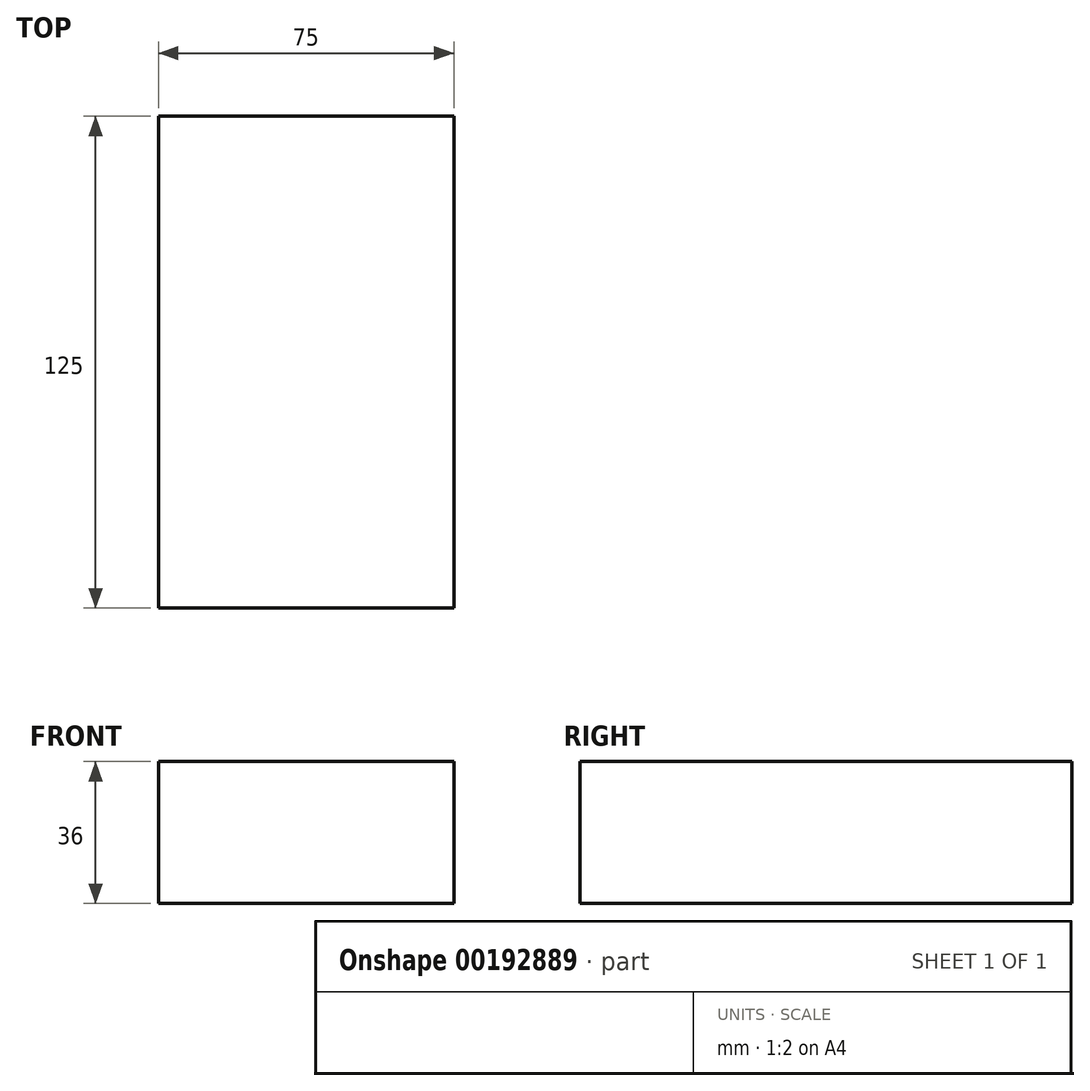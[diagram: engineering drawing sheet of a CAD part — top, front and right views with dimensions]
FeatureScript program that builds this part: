
annotation { "Feature Type Name" : "Feature", "Feature Type Description" : "" }
export const myFeature = defineFeature(function(context is Context, id is Id, definition is map)
    precondition{}
    {
        {
            var Q0;
            Q0=qCreatedBy(makeId("Front.planeOp"),FACE);
            var sketch = newSketch(context, id + "F0", { "sketchPlane" : qUnion([Q0])});
            skLineSegment(sketch, "E0.bottom", {"start": v(-37.5, 18) * mm, "end": v(37.5, 18) * mm});
            skLineSegment(sketch, "E0.top", {"start": v(-37.5, -18) * mm, "end": v(37.5, -18) * mm});
            skLineSegment(sketch, "E0.left", {"start": v(-37.5, 18) * mm, "end": v(-37.5, -18) * mm});
            skLineSegment(sketch, "E0.right", {"start": v(37.5, 18) * mm, "end": v(37.5, -18) * mm});
            skPoint(sketch, "E0.middle", {"position": v(0, 0) * mm});
            skSolve(sketch);
        }
        {
            var Q0;
            Q0=makeQuery(id+"F0.imprint","IMPRINT",FACE,{"disambiguationData":[TD([[makeQuery(id+"F0.imprint","IMPRINT",EDGE,{"derivedFrom":sQuery(id+"F0.wireOp",EDGE,"E0.bottom")}),-1.0]])]});
            extrude(context, id + "F1", {"entities" : qUnion([Q0]), "endBound" : BoundingType.SYMMETRIC, "depth" : 125 * mm});
        }
    });
